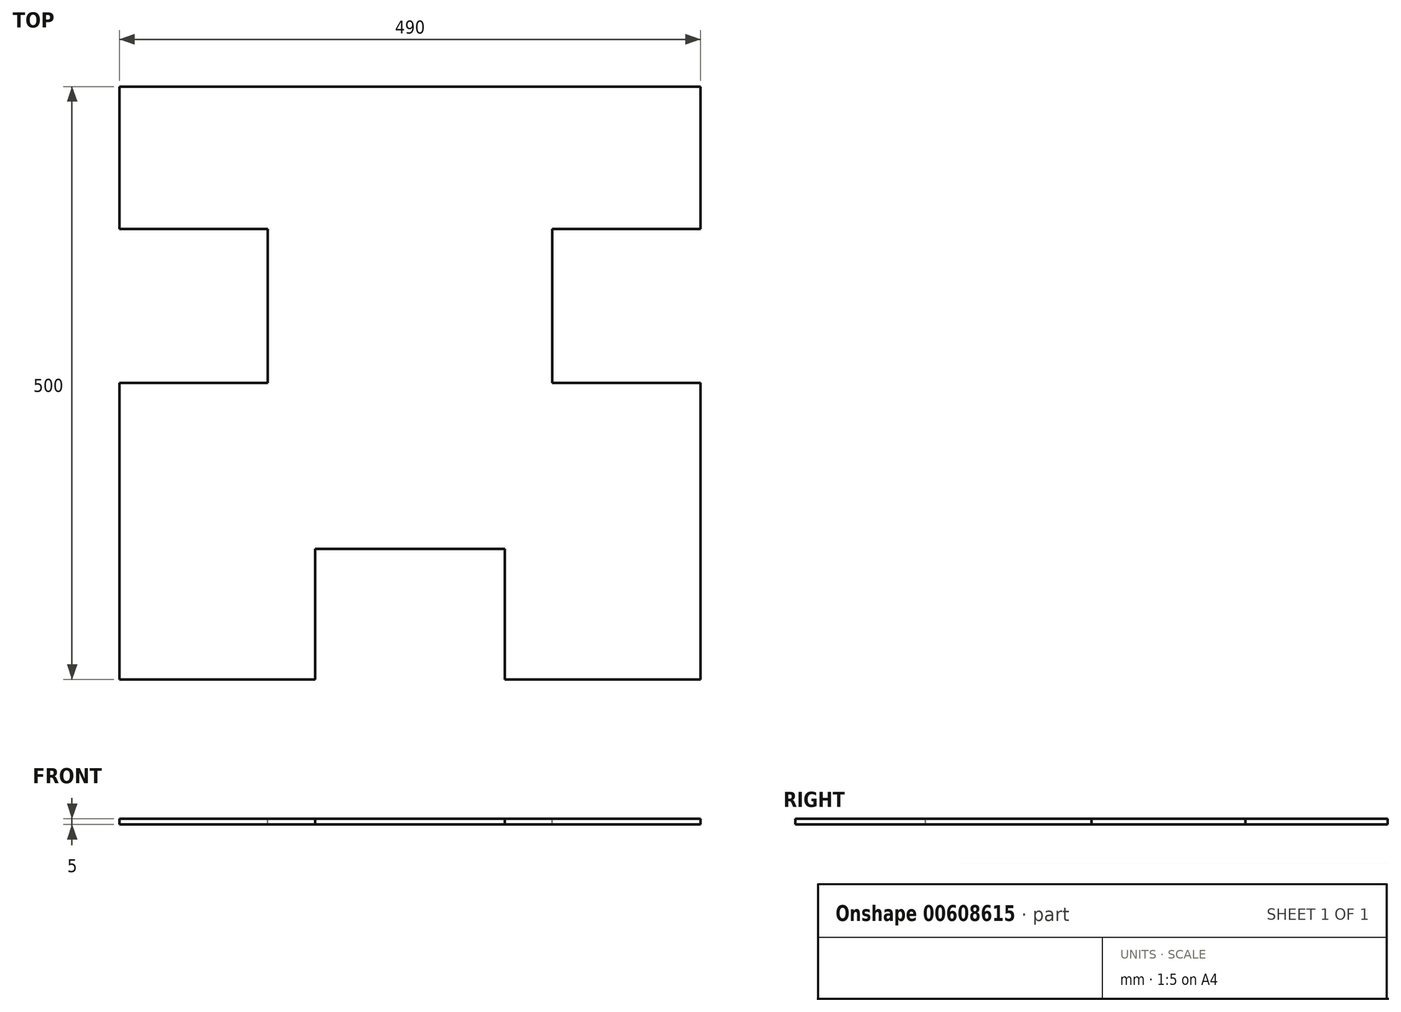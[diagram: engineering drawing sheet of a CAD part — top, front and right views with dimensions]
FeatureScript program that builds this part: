
annotation { "Feature Type Name" : "Feature", "Feature Type Description" : "" }
export const myFeature = defineFeature(function(context is Context, id is Id, definition is map)
    precondition{}
    {
        {
            var Q0;
            Q0=qCreatedBy(makeId("Top.planeOp"),FACE);
            var sketch = newSketch(context, id + "F0", { "sketchPlane" : qUnion([Q0])});
            skLineSegment(sketch, "E0.bottom", {"start": v(0, 0) * mm, "end": v(490, 0) * mm});
            skLineSegment(sketch, "E0.top", {"start": v(0, 500) * mm, "end": v(490, 500) * mm});
            skLineSegment(sketch, "E0.left", {"start": v(0, 0) * mm, "end": v(0, 500) * mm});
            skLineSegment(sketch, "E0.right", {"start": v(490, 0) * mm, "end": v(490, 500) * mm});
            skSolve(sketch);
        }
        {
            var Q0;
            Q0 = qSketchRegion(id + "F0", true);
            extrude(context, id + "F1", {"entities" : qUnion([Q0]), "depth" : 5 * mm, "offsetDistance" : 25 * mm});
        }
        {
            var Q0;
            Q0=makeQuery(id+"F1.opExtrude","CAP_FACE",FACE,{"disambiguationData":[OSD([sQuery(id+"F0.wireOp",EDGE,"E0.bottom"),sQuery(id+"F0.wireOp",EDGE,"E0.top"),sQuery(id+"F0.wireOp",EDGE,"E0.left"),sQuery(id+"F0.wireOp",EDGE,"E0.right")])],"isStart":false});
            var sketch = newSketch(context, id + "F2", { "sketchPlane" : qUnion([Q0])});
            skLineSegment(sketch, "E1.bottom", {"start": v(165, 0) * mm, "end": v(325, 0) * mm});
            skLineSegment(sketch, "E1.top", {"start": v(165, 110) * mm, "end": v(325, 110) * mm});
            skLineSegment(sketch, "E1.left", {"start": v(165, 0) * mm, "end": v(165, 110) * mm});
            skLineSegment(sketch, "E1.right", {"start": v(325, 0) * mm, "end": v(325, 110) * mm});
            skLineSegment(sketch, "E2.bottom", {"start": v(0, 250) * mm, "end": v(125, 250) * mm});
            skLineSegment(sketch, "E2.top", {"start": v(0, 380) * mm, "end": v(125, 380) * mm});
            skLineSegment(sketch, "E2.left", {"start": v(0, 250) * mm, "end": v(0, 380) * mm});
            skLineSegment(sketch, "E2.right", {"start": v(125, 250) * mm, "end": v(125, 380) * mm});
            skLineSegment(sketch, "E3.bottom", {"start": v(490, 250) * mm, "end": v(365, 250) * mm});
            skLineSegment(sketch, "E3.top", {"start": v(490, 380) * mm, "end": v(365, 380) * mm});
            skLineSegment(sketch, "E3.left", {"start": v(490, 250) * mm, "end": v(490, 380) * mm});
            skLineSegment(sketch, "E3.right", {"start": v(365, 250) * mm, "end": v(365, 380) * mm});
            skSolve(sketch);
        }
        {
            var Q0;
            Q0 = qSketchRegion(id + "F2", true);
            extrude(context, id + "F3", {"entities" : qUnion([Q0]), "operationType" : NewBodyOperationType.REMOVE, "oppositeDirection" : true, "depth" : 25 * mm, "offsetDistance" : 25 * mm});
        }
    });
